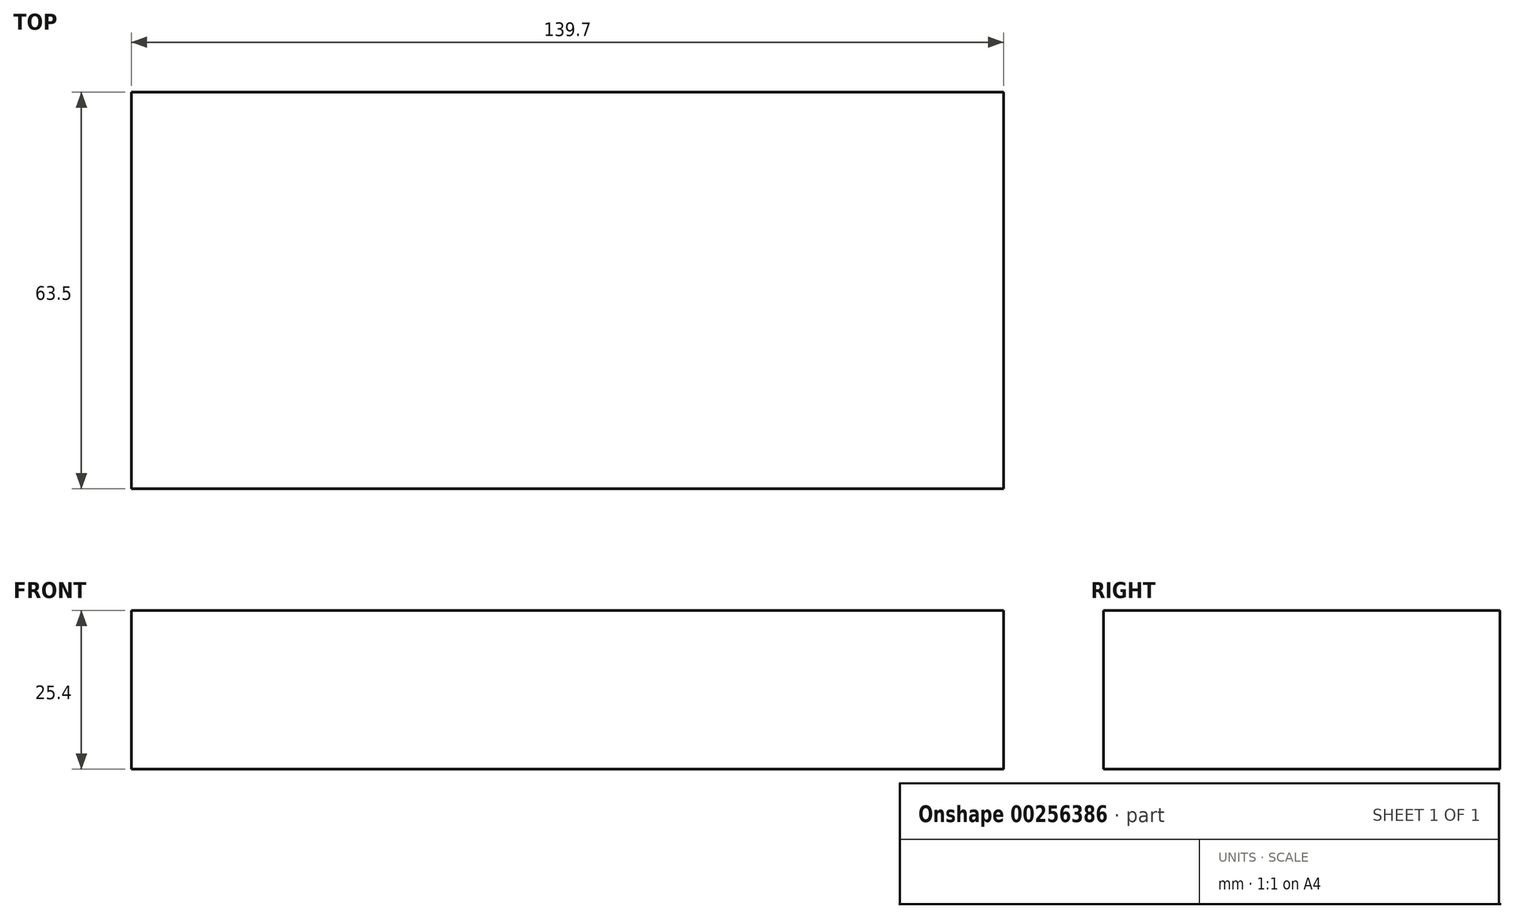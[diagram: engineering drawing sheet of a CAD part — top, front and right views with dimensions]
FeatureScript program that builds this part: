
annotation { "Feature Type Name" : "Feature", "Feature Type Description" : "" }
export const myFeature = defineFeature(function(context is Context, id is Id, definition is map)
    precondition{}
    {
        {
            var Q0;
            Q0=qCreatedBy(makeId("Top.planeOp"),FACE);
            var sketch = newSketch(context, id + "F0", { "sketchPlane" : qUnion([Q0])});
            skLineSegment(sketch, "E0.bottom", {"start": v(-54.75, 38.38) * mm, "end": v(84.95, 38.38) * mm});
            skLineSegment(sketch, "E0.top", {"start": v(-54.75, -25.12) * mm, "end": v(84.95, -25.12) * mm});
            skLineSegment(sketch, "E0.left", {"start": v(-54.75, 38.38) * mm, "end": v(-54.75, -25.12) * mm});
            skLineSegment(sketch, "E0.right", {"start": v(84.95, 38.38) * mm, "end": v(84.95, -25.12) * mm});
            skSolve(sketch);
        }
        {
            var Q0;
            Q0 = qSketchRegion(id + "F0", true);
            extrude(context, id + "F1", {"entities" : qUnion([Q0]), "depth" : 25.4 * mm});
        }
    });
